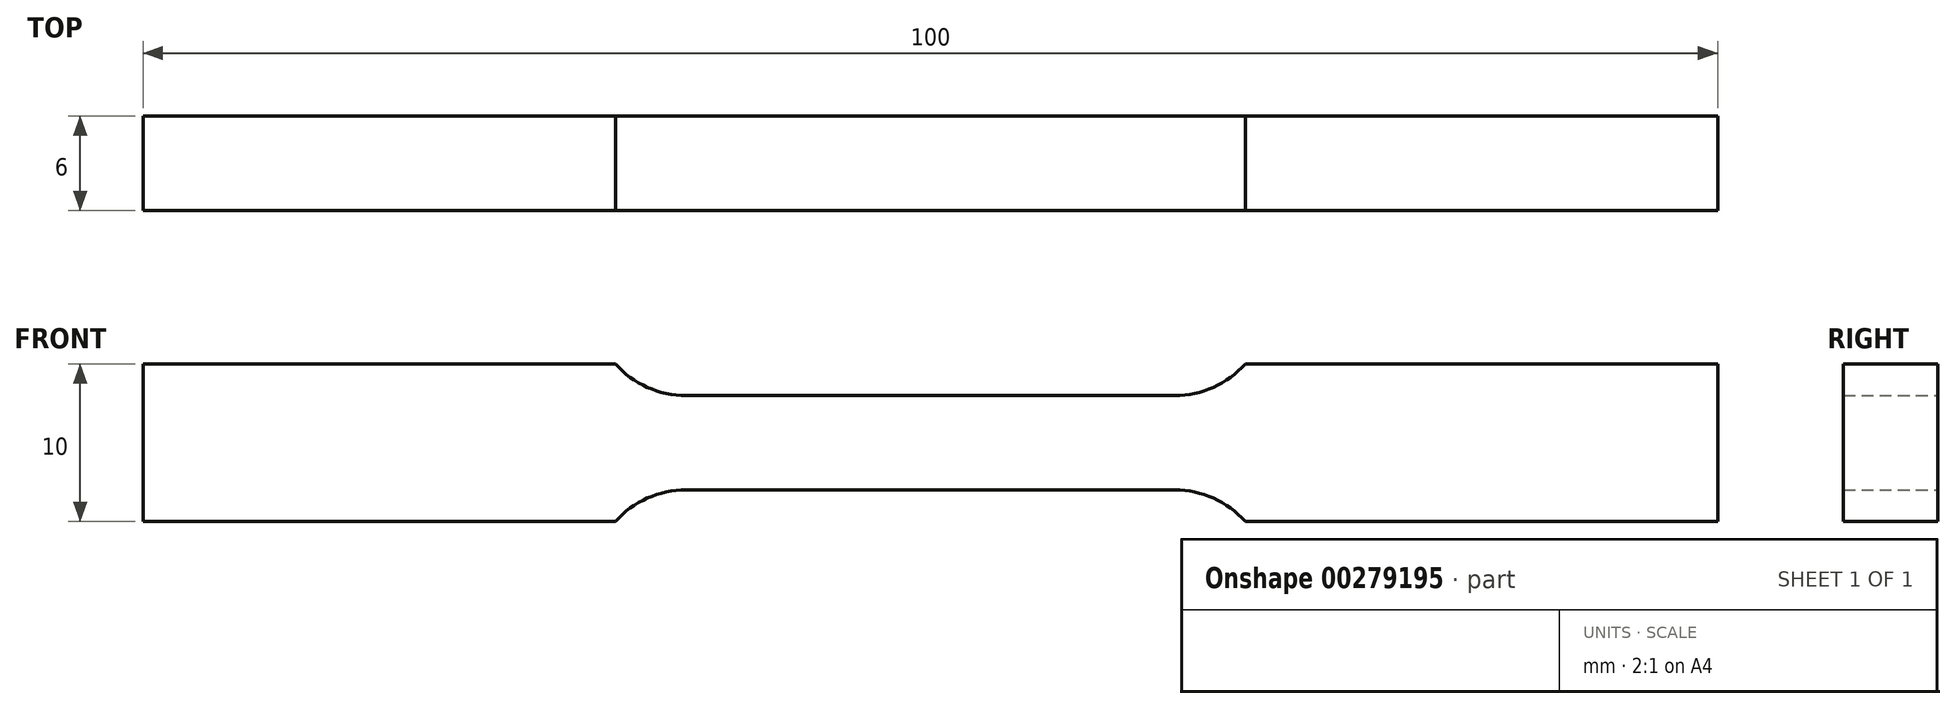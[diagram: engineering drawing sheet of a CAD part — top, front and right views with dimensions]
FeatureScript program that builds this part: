
annotation { "Feature Type Name" : "Feature", "Feature Type Description" : "" }
export const myFeature = defineFeature(function(context is Context, id is Id, definition is map)
    precondition{}
    {
        {
            var Q0;
            Q0=qCreatedBy(makeId("Front.planeOp"),FACE);
            var sketch = newSketch(context, id + "F0", { "sketchPlane" : qUnion([Q0])});
            skLineSegment(sketch, "E0", {"start": v(0, 3) * mm, "end": v(15.53, 3) * mm});
            skArc(sketch, "E1", {"start": v(15.53, 3) * mm, "mid": v(17.98, 3.52) * mm, "end": v(20, 5) * mm});
            skLineSegment(sketch, "E2", {"start": v(20, 5) * mm, "end": v(50, 5) * mm});
            skLineSegment(sketch, "E3", {"start": v(50, 5) * mm, "end": v(50, 0) * mm});
            skLineSegment(sketch, "E4.MirrorCS", {"start": v(0, -3) * mm, "end": v(15.53, -3) * mm});
            skLineSegment(sketch, "E5.MirrorCS", {"start": v(50, -5) * mm, "end": v(50, 0) * mm});
            skLineSegment(sketch, "E6.MirrorCS", {"start": v(20, -5) * mm, "end": v(50, -5) * mm});
            skArc(sketch, "E7.MirrorCS", {"start": v(15.53, -3) * mm, "mid": v(17.98, -3.52) * mm, "end": v(20, -5) * mm});
            skArc(sketch, "E8.MirrorCS", {"start": v(-15.53, -3) * mm, "mid": v(-17.98, -3.52) * mm, "end": v(-20, -5) * mm});
            skArc(sketch, "E9.MirrorCS", {"start": v(-15.53, 3) * mm, "mid": v(-17.98, 3.52) * mm, "end": v(-20, 5) * mm});
            skLineSegment(sketch, "E10.MirrorCS", {"start": v(-20, -5) * mm, "end": v(-50, -5) * mm});
            skLineSegment(sketch, "E11.MirrorCS", {"start": v(-20, 5) * mm, "end": v(-50, 5) * mm});
            skLineSegment(sketch, "E12.MirrorCS", {"start": v(-50, -5) * mm, "end": v(-50, 0) * mm});
            skLineSegment(sketch, "E13.MirrorCS", {"start": v(0, -3) * mm, "end": v(-15.53, -3) * mm});
            skLineSegment(sketch, "E14.MirrorCS", {"start": v(-50, 5) * mm, "end": v(-50, 0) * mm});
            skLineSegment(sketch, "E15.MirrorCS", {"start": v(0, 3) * mm, "end": v(-15.53, 3) * mm});
            skSolve(sketch);
        }
        {
            var Q0;
            Q0 = qSketchRegion(id + "F0", true);
            extrude(context, id + "F1", {"entities" : qUnion([Q0]), "endBound" : BoundingType.SYMMETRIC, "depth" : 6 * mm});
        }
    });
